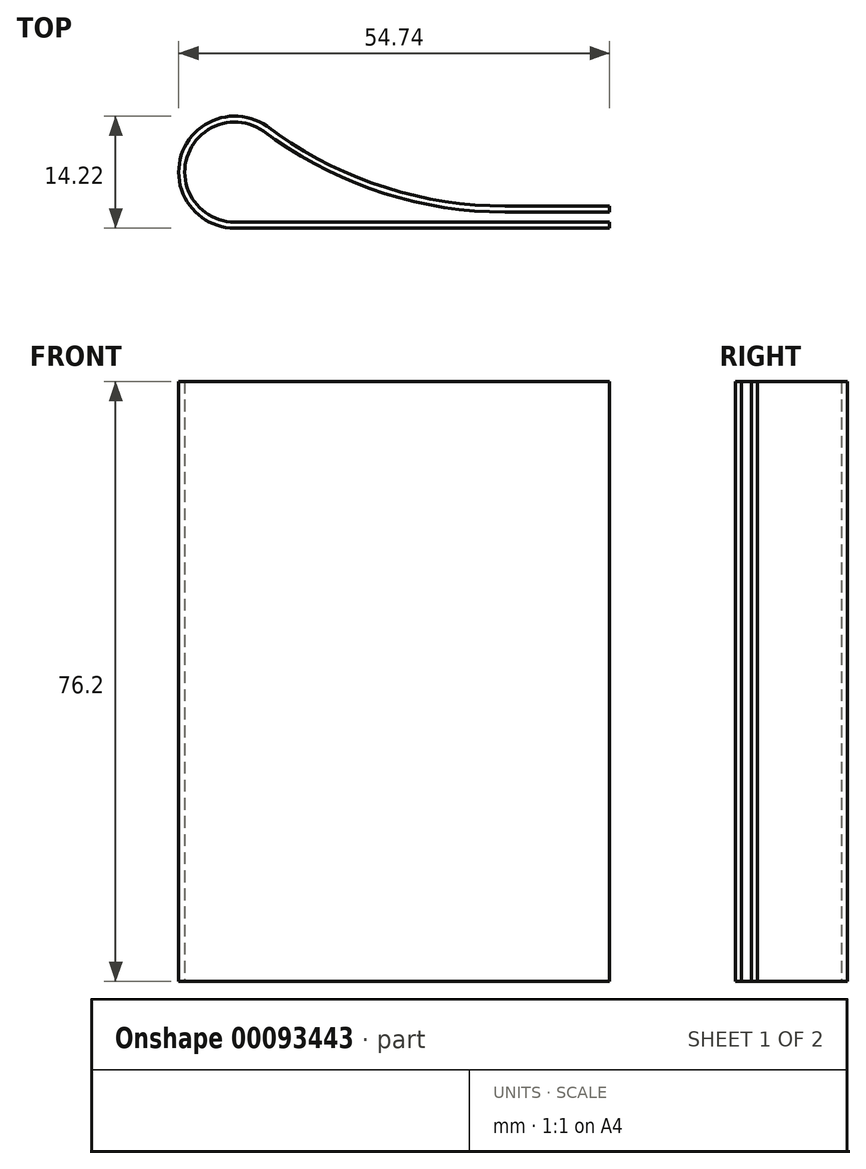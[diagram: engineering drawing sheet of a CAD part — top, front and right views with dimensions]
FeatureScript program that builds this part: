
annotation { "Feature Type Name" : "Feature", "Feature Type Description" : "" }
export const myFeature = defineFeature(function(context is Context, id is Id, definition is map)
    precondition{}
    {
        {
            var Q0;
            Q0=qCreatedBy(makeId("Top.planeOp"),FACE);
            var sketch = newSketch(context, id + "F0", { "sketchPlane" : qUnion([Q0])});
            skLineSegment(sketch, "E0", {"start": v(0, 0) * mm, "end": v(-47.63, 0) * mm});
            skLineSegment(sketch, "E1", {"start": v(-53.98, 6.35) * mm, "end": v(-53.98, 6.35) * mm});
            skLineSegment(sketch, "E2", {"start": v(-43.98, 11.55) * mm, "end": v(-42.48, 10.5) * mm});
            skLineSegment(sketch, "E3", {"start": v(-13.29, 1.27) * mm, "end": v(0, 1.27) * mm});
            skPoint(sketch, "E4.visualSharp", {"position": v(-53.98, 0) * mm});
            skArc(sketch, "E4.filletArc", {"start": v(-53.98, 6.35) * mm, "mid": v(-52.12, 1.86) * mm, "end": v(-47.63, 0) * mm});
            skPoint(sketch, "E5.visualSharp", {"position": v(-29.34, 1.27) * mm});
            skArc(sketch, "E5.filletArc", {"start": v(-42.48, 10.5) * mm, "mid": v(-28.6, 3.63) * mm, "end": v(-13.29, 1.27) * mm});
            skPoint(sketch, "E6.visualSharp", {"position": v(-53.98, 18.57) * mm});
            skArc(sketch, "E6.filletArc", {"start": v(-43.98, 11.55) * mm, "mid": v(-50.55, 11.98) * mm, "end": v(-53.98, 6.35) * mm});
            skLineSegment(sketch, "E7.0", {"start": v(0, -0.76) * mm, "end": v(-47.63, -0.76) * mm});
            skArc(sketch, "E7.1", {"start": v(-54.74, 6.35) * mm, "mid": v(-52.65, 1.32) * mm, "end": v(-47.63, -0.76) * mm});
            skLineSegment(sketch, "E7.2", {"start": v(-13.29, 2.03) * mm, "end": v(0, 2.03) * mm});
            skArc(sketch, "E7.3", {"start": v(-42.04, 11.12) * mm, "mid": v(-28.36, 4.36) * mm, "end": v(-13.29, 2.03) * mm});
            skLineSegment(sketch, "E7.4", {"start": v(-43.54, 12.17) * mm, "end": v(-42.04, 11.12) * mm});
            skArc(sketch, "E7.5", {"start": v(-43.54, 12.17) * mm, "mid": v(-50.9, 12.66) * mm, "end": v(-54.74, 6.35) * mm});
            skLineSegment(sketch, "E8", {"start": v(0, -0.76) * mm, "end": v(0, 0) * mm});
            skLineSegment(sketch, "E9", {"start": v(0, 1.27) * mm, "end": v(0, 2.03) * mm});
            skSolve(sketch);
        }
        {
            var Q0;
            Q0 = qSketchRegion(id + "F0", true);
            extrude(context, id + "F1", {"entities" : qUnion([Q0]), "depth" : 76.2 * mm});
        }
    });
